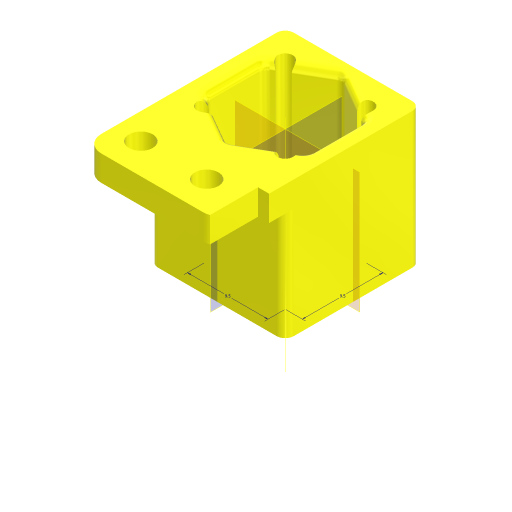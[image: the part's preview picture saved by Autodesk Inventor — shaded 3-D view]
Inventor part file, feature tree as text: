
AUTODESK INVENTOR PART (.ipt)
format: ipt  version: 2024.1 (Build 281209000, 209)  size: 273,920 bytes
history: native  units: mm
features: extrude x4, other x3, sketch x3, projected_geometry x3, fillet x2, plane x2, reference x1
ambient origin geometry x8: Origin, YZ Plane, XZ Plane, XY Plane, X Axis, Y Axis, Z Axis, Center Point
bodies: Volumenkörper1 (feature_tree)
feature tree (18):
  extrude  "Extrusion1"  Depth=16.0mm
  fillet  "Rundung1"  Radius=3.0mm
  extrude  "Extrusion2"  Depth=13.0mm
  fillet  "Rundung2"  Radius=13.0mm
  other  "Arbeitsachse1"
  extrude  "Extrusion3"  Depth=10.0mm
  extrude  "Extrusion4"  Depth=3.0mm
  sketch  "Skizze5"  dims[d9=1.0mm d10=10.0mm d11=2.8mm d12=2.8mm d13=2.0mm d14=3.0mm d15=0.0mm d16=0.1mm d17=0.0mm d18=0.0mm d19=9.5mm d20=9.5mm d21=6.0mm d22=9.5mm d23=9.5mm d24=1.8mm d25=1.8mm d26=1.8mm d27=1.8mm]
  sketch  "Skizze2"  dims[d0=16.0mm d1=16.0mm d3=3.0mm d4=0.0mm]
  projected_geometry  "Projizierte Kontur1"
  plane  "Arbeitsebene1"
  plane  "Arbeitsebene2"
  sketch  "Skizze3"  dims[d5=2.0mm d6=11.85mm d7=13.0mm d8=0.0mm]
  projected_geometry  "Projizierte Kontur2"
  reference  "Referenz1"
  projected_geometry  "Projizierte Kontur3"
  other  "Assemlby_lightsheet_generator_passive_v2.iam"
  other  "30_Lightsheet_generator_passive_lid_v1:1"
